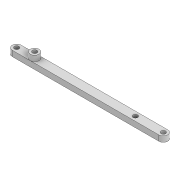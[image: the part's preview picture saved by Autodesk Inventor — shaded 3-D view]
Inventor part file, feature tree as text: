
AUTODESK INVENTOR PART (.ipt)
format: ipt  version: 2022 (Build 260153000, 153)  size: 109,568 bytes
history: native  units: mm
features: extrude x2, sketch x1, projected_geometry x1
ambient origin geometry x8: Origin, YZ Plane, XZ Plane, XY Plane, X Axis, Y Axis, Z Axis, Center Point
bodies: Solid1 (feature_tree)
feature tree (4):
  extrude  "Extrusion1"  Depth=8.0mm
  extrude  "Extrusion7"  Depth=5.0mm
  sketch  "Sketch4"  dims[d0=132.537mm d1=8.0mm d2=4.2mm d4=5.0mm d5=0.0mm d8=4.2mm d9=16.286mm d10=4.2mm d28=4.2mm d29=107.252mm d30=8.0mm d31=5.0mm d32=0.0mm]
  projected_geometry  "Projected Loop3"
